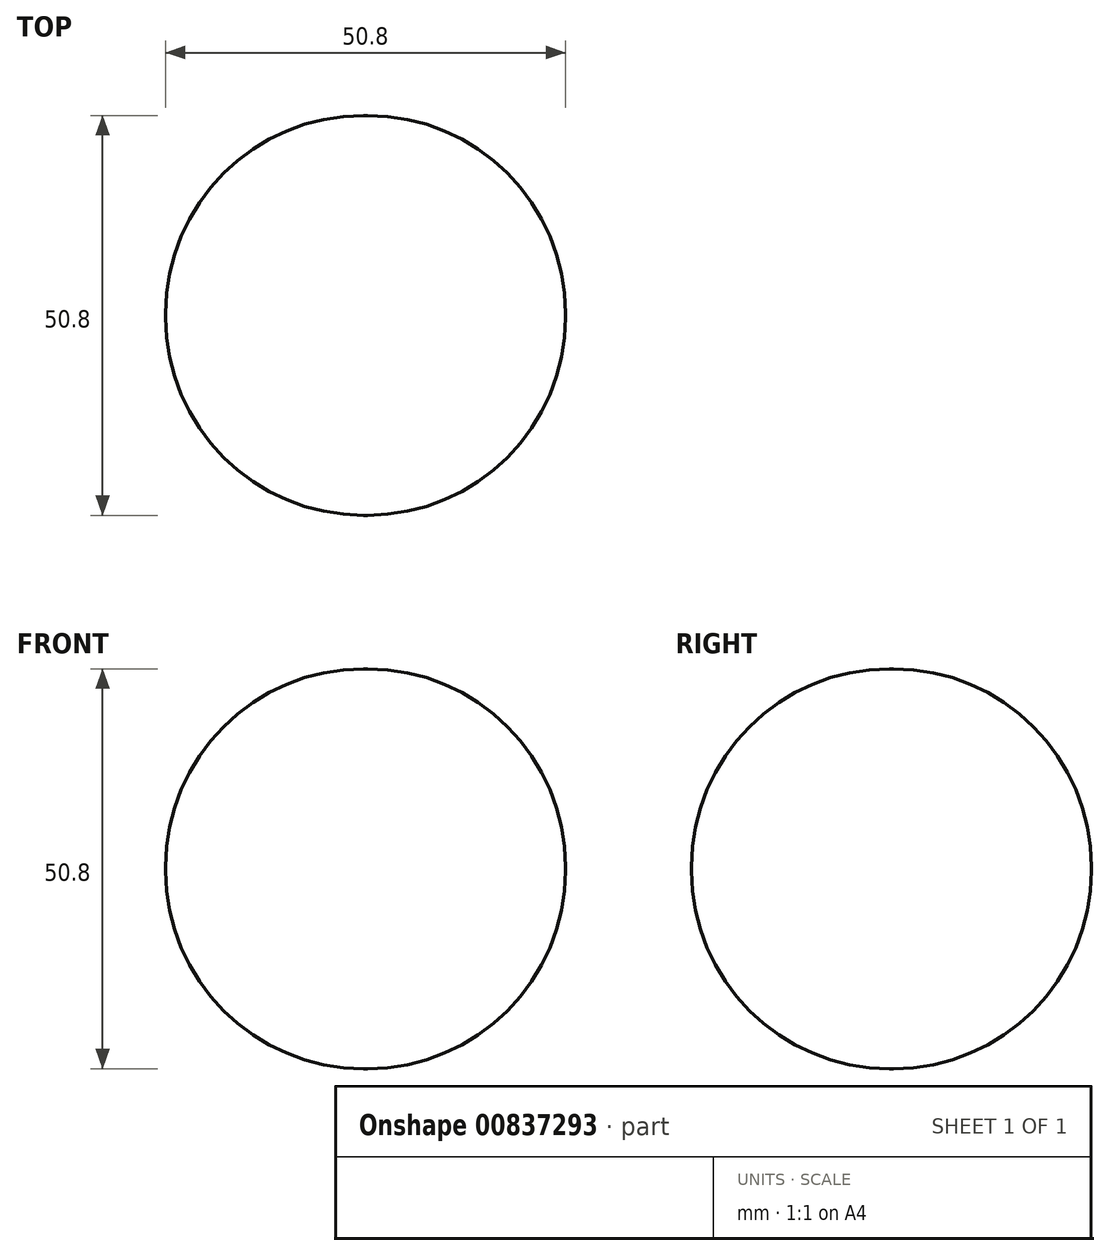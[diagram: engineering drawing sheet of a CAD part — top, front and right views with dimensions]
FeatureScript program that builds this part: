
annotation { "Feature Type Name" : "Feature", "Feature Type Description" : "" }
export const myFeature = defineFeature(function(context is Context, id is Id, definition is map)
    precondition{}
    {
        {
            var Q0;
            Q0=qCreatedBy(makeId("Top.planeOp"),FACE);
            var sketch = newSketch(context, id + "F0", { "sketchPlane" : qUnion([Q0])});
            skLineSegment(sketch, "E0.bottom", {"start": v(25.4, 25.4) * mm, "end": v(-25.4, 25.4) * mm});
            skLineSegment(sketch, "E0.top", {"start": v(25.4, -25.4) * mm, "end": v(-25.4, -25.4) * mm});
            skLineSegment(sketch, "E0.left", {"start": v(25.4, 25.4) * mm, "end": v(25.4, -25.4) * mm});
            skLineSegment(sketch, "E0.right", {"start": v(-25.4, 25.4) * mm, "end": v(-25.4, -25.4) * mm});
            skPoint(sketch, "E0.middle", {"position": v(0, 0) * mm});
            skSolve(sketch);
        }
        {
            var Q0;
            Q0=makeQuery(id+"F0.imprint","IMPRINT",FACE,{"disambiguationData":[TD([[makeQuery(id+"F0.imprint","IMPRINT",EDGE,{"derivedFrom":sQuery(id+"F0.wireOp",EDGE,"E0.bottom")}),1.0]])]});
            extrude(context, id + "F1", {"entities" : qUnion([Q0]), "depth" : 50.8 * mm, "offsetDistance" : 25.4 * mm});
        }
        {
            var Q0;
            Q0=makeQuery(id+"F1.opExtrude","CAP_EDGE",EDGE,{"disambiguationData":[OSD([sQuery(id+"F0.wireOp",EDGE,"E0.right")])],"isStart":false});
            var Q1;
            Q1=makeQuery(id+"F1.opExtrude","CAP_EDGE",EDGE,{"disambiguationData":[OSD([sQuery(id+"F0.wireOp",EDGE,"E0.left")])],"isStart":false});
            var Q2;
            Q2=makeQuery(id+"F1.opExtrude","CAP_EDGE",EDGE,{"disambiguationData":[OSD([sQuery(id+"F0.wireOp",EDGE,"E0.right")])],"isStart":true});
            var Q3;
            Q3=makeQuery(id+"F1.opExtrude","CAP_EDGE",EDGE,{"disambiguationData":[OSD([sQuery(id+"F0.wireOp",EDGE,"E0.left")])],"isStart":true});
            var Q4;
            Q4=makeQuery(id+"F1.opExtrude","SWEPT_EDGE",EDGE,{"disambiguationData":[OSD([sQuery(id+"F0.wireOp",EDGE,"E0.top"),sQuery(id+"F0.wireOp",EDGE,"E0.right")])]});
            var Q5;
            Q5=makeQuery(id+"F1.opExtrude","SWEPT_EDGE",EDGE,{"disambiguationData":[OSD([sQuery(id+"F0.wireOp",EDGE,"E0.top"),sQuery(id+"F0.wireOp",EDGE,"E0.left")])]});
            var Q6;
            Q6=makeQuery(id+"F1.opExtrude","CAP_EDGE",EDGE,{"disambiguationData":[OSD([sQuery(id+"F0.wireOp",EDGE,"E0.top")])],"isStart":true});
            var Q7;
            Q7=makeQuery(id+"F1.opExtrude","CAP_EDGE",EDGE,{"disambiguationData":[OSD([sQuery(id+"F0.wireOp",EDGE,"E0.top")])],"isStart":false});
            var Q8;
            Q8=makeQuery(id+"F1.opExtrude","SWEPT_EDGE",EDGE,{"disambiguationData":[OSD([sQuery(id+"F0.wireOp",EDGE,"E0.bottom"),sQuery(id+"F0.wireOp",EDGE,"E0.right")])]});
            var Q9;
            Q9=makeQuery(id+"F1.opExtrude","CAP_EDGE",EDGE,{"disambiguationData":[OSD([sQuery(id+"F0.wireOp",EDGE,"E0.bottom")])],"isStart":true});
            var Q10;
            Q10=makeQuery(id+"F1.opExtrude","SWEPT_EDGE",EDGE,{"disambiguationData":[OSD([sQuery(id+"F0.wireOp",EDGE,"E0.bottom"),sQuery(id+"F0.wireOp",EDGE,"E0.left")])]});
            var Q11;
            Q11=makeQuery(id+"F1.opExtrude","CAP_EDGE",EDGE,{"disambiguationData":[OSD([sQuery(id+"F0.wireOp",EDGE,"E0.bottom")])],"isStart":false});
            fillet(context, id + "F2", {"entities" : qUnion([Q0, Q1, Q2, Q3, Q4, Q5, Q6, Q7, Q8, Q9, Q10, Q11]), "radius" : 25.15 * mm, "tangentPropagation" : true, "allowEdgeOverflow" : false});
        }
    });
